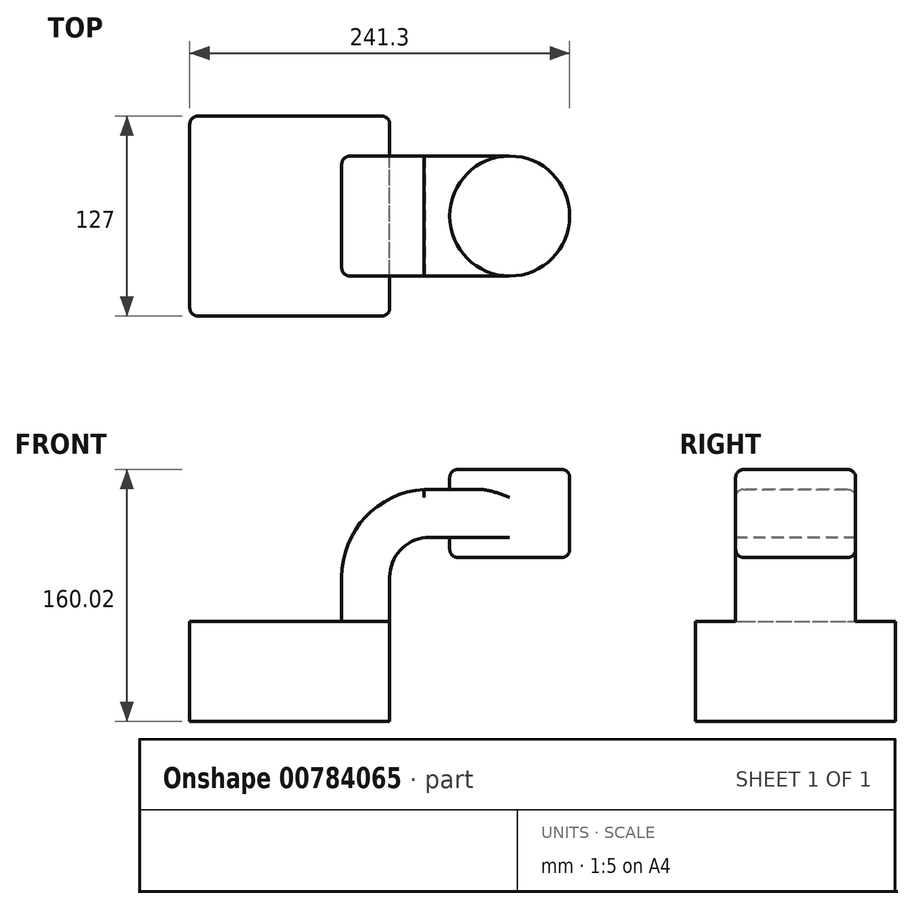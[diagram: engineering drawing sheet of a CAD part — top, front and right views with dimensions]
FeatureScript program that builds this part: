
annotation { "Feature Type Name" : "Feature", "Feature Type Description" : "" }
export const myFeature = defineFeature(function(context is Context, id is Id, definition is map)
    precondition{}
    {
        {
            var Q0;
            Q0=qCreatedBy(makeId("Front.planeOp"),FACE);
            var sketch = newSketch(context, id + "F0", { "sketchPlane" : qUnion([Q0])});
            skLineSegment(sketch, "E0.bottom", {"start": v(63.5, 31.75) * mm, "end": v(-63.5, 31.75) * mm});
            skLineSegment(sketch, "E0.top", {"start": v(63.5, -31.75) * mm, "end": v(-63.5, -31.75) * mm});
            skLineSegment(sketch, "E0.left", {"start": v(63.5, 31.75) * mm, "end": v(63.5, -31.75) * mm});
            skLineSegment(sketch, "E0.right", {"start": v(-63.5, 31.75) * mm, "end": v(-63.5, -31.75) * mm});
            skPoint(sketch, "E0.middle", {"position": v(0, 0) * mm});
            skLineSegment(sketch, "E1.bottom", {"start": v(177.8, 128.27) * mm, "end": v(101.6, 128.27) * mm});
            skLineSegment(sketch, "E1.top", {"start": v(177.8, 72.4) * mm, "end": v(101.6, 72.4) * mm});
            skLineSegment(sketch, "E1.left", {"start": v(177.8, 128.27) * mm, "end": v(177.8, 72.4) * mm});
            skLineSegment(sketch, "E1.right", {"start": v(101.6, 128.27) * mm, "end": v(101.6, 72.4) * mm});
            skPoint(sketch, "E1.middle", {"position": v(139.7, 100.33) * mm});
            skLineSegment(sketch, "E2", {"start": v(63.5, 31.75) * mm, "end": v(63.5, 59.92) * mm});
            skArc(sketch, "E3", {"start": v(63.5, 59.92) * mm, "mid": v(70.06, 76.96) * mm, "end": v(86.36, 85.2) * mm});
            skLineSegment(sketch, "E4", {"start": v(86.36, 85.2) * mm, "end": v(139.7, 85.2) * mm});
            skLineSegment(sketch, "E5.0", {"start": v(85.13, 115.68) * mm, "end": v(139.7, 115.68) * mm});
            skArc(sketch, "E5.1", {"start": v(33.02, 59.92) * mm, "mid": v(48.08, 98.08) * mm, "end": v(85.13, 115.68) * mm});
            skLineSegment(sketch, "E5.2", {"start": v(33.02, 31.75) * mm, "end": v(33.02, 59.92) * mm});
            skLineSegment(sketch, "E6", {"start": v(139.7, 72.4) * mm, "end": v(139.7, 128.27) * mm});
            skFitSpline(sketch, "E7", {"points": [v(-63.5, 31.75) * mm, v(85.13, 115.68) * mm], "startDerivative": vector(64.72, 185.3) * mm, "endDerivative": vector(169.63, -1.96) * mm});
            skSolve(sketch);
        }
        {
            var Q0;
            Q0=makeQuery(id+"F0.imprint","IMPRINT",FACE,{"disambiguationData":[TD([[makeQuery(id+"F0.imprint","IMPRINT",EDGE,{"derivedFrom":sQuery(id+"F0.wireOp",EDGE,"E0.top")}),-1.0]])]});
            extrude(context, id + "F1", {"entities" : qUnion([Q0]), "endBound" : BoundingType.SYMMETRIC, "depth" : 127 * mm, "offsetDistance" : 25.4 * mm});
        }
        {
            var Q0;
            {var subQ1=sQuery(id+"F0.wireOp",EDGE,"E2");Q0=makeQuery(id+"F0.imprint","IMPRINT",FACE,{"disambiguationData":[TD([[makeQuery(id+"F0.imprint","IMPRINT",EDGE,{"derivedFrom":subQ1}),1.0]])]});}
            extrude(context, id + "F2", {"entities" : qUnion([Q0]), "operationType" : NewBodyOperationType.ADD, "endBound" : BoundingType.SYMMETRIC, "depth" : 76.2 * mm, "offsetDistance" : 25.4 * mm});
        }
        {
            var Q0;
            Q0=makeQuery(id+"F0.imprint","IMPRINT",FACE,{"disambiguationData":[TD([[makeQuery(id+"F0.imprint","IMPRINT",EDGE,{"derivedFrom":sQuery(id+"F0.wireOp",EDGE,"E5.1")}),1.0]])]});
            extrude(context, id + "F3", {"entities" : qUnion([Q0]), "operationType" : NewBodyOperationType.ADD, "endBound" : BoundingType.SYMMETRIC, "depth" : 19.05 * mm, "offsetDistance" : 25.4 * mm});
        }
        {
            var Q0;
            {var subQ0=sQuery(id+"F0.wireOp",EDGE,"E5.0");var subQ1=sQuery(id+"F0.wireOp",EDGE,"E1.right");var subQ2=makeQuery(id+"F0.imprint","INTERSECT",VERTEX,{"derivedFrom":[subQ1,subQ0]});Q0=makeQuery(id+"F0.imprint","IMPRINT",FACE,{"disambiguationData":[TD([[makeQuery(id+"F0.imprint","IMPRINT",EDGE,{"disambiguationData":[TD([[subQ2,-1.0]])],"derivedFrom":subQ1}),1.0]])]});}
            extrude(context, id + "F4", {"entities" : qUnion([Q0]), "operationType" : NewBodyOperationType.ADD, "endBound" : BoundingType.SYMMETRIC, "depth" : 76.2 * mm, "offsetDistance" : 25.4 * mm});
        }
        {
            var Q0;
            {var subQ4=sQuery(id+"F0.wireOp",EDGE,"E1.left");Q0=makeQuery(id+"F0.imprint","IMPRINT",FACE,{"disambiguationData":[TD([[makeQuery(id+"F0.imprint","IMPRINT",EDGE,{"derivedFrom":subQ4}),-1.0]])]});}
            var Q1;
            Q1=sQuery(id+"F0.wireOp",EDGE,"E6");
            revolve(context, id + "F5", {"operationType" : NewBodyOperationType.ADD, "surfaceOperationType" : NewSurfaceOperationType.NEW, "entities" : qUnion([Q0]), "axis" : qUnion([Q1]), "revolveType" : RevolveType.FULL});
        }
        {
            var Q0;
            Q0=makeQuery(id+"F1.opExtrude","CAP_EDGE",EDGE,{"disambiguationData":[OSD([sQuery(id+"F0.wireOp",EDGE,"E0.left")])],"isStart":false});
            var Q1;
            Q1=makeQuery(id+"F1.opExtrude","CAP_EDGE",EDGE,{"disambiguationData":[OSD([sQuery(id+"F0.wireOp",EDGE,"E0.right")])],"isStart":false});
            var Q2;
            Q2=makeQuery(id+"F3.opExtrude","CAP_EDGE",EDGE,{"disambiguationData":[OSD([sQuery(id+"F0.wireOp",EDGE,"E7")])],"isStart":false});
            var Q3;
            Q3=makeQuery(id+"F1.opExtrude","CAP_EDGE",EDGE,{"disambiguationData":[OSD([sQuery(id+"F0.wireOp",EDGE,"E0.left")])],"isStart":true});
            var Q4;
            Q4=makeQuery(id+"F3.opExtrude","CAP_EDGE",EDGE,{"disambiguationData":[OSD([sQuery(id+"F0.wireOp",EDGE,"E7")])],"isStart":true});
            var Q5;
            Q5=makeQuery(id+"F1.opExtrude","CAP_EDGE",EDGE,{"disambiguationData":[OSD([sQuery(id+"F0.wireOp",EDGE,"E0.right")])],"isStart":true});
            var Q6;
            Q6=makeQuery(id+"F2.opExtrude","CAP_EDGE",EDGE,{"disambiguationData":[OSD([sQuery(id+"F0.wireOp",EDGE,"E5.1")])],"isStart":true});
            var Q7;
            Q7=makeQuery(id+"F2.opExtrude","CAP_EDGE",EDGE,{"disambiguationData":[OSD([sQuery(id+"F0.wireOp",EDGE,"E5.2")])],"isStart":true});
            var Q8;
            {var subQ0=sQuery(id+"F0.wireOp",EDGE,"E5.0");Q8=makeQuery(id+"F4.boolean.opBoolean","MERGE",EDGE,{"derivedFrom":[makeQuery(id+"F2.opExtrude","CAP_EDGE",EDGE,{"disambiguationData":[OSD([subQ0])],"isStart":true}),makeQuery(id+"F4.opExtrude","CAP_EDGE",EDGE,{"disambiguationData":[OSD([subQ0])],"isStart":true})]});}
            var Q9;
            Q9=makeQuery(id+"F2.opExtrude","CAP_EDGE",EDGE,{"disambiguationData":[OSD([sQuery(id+"F0.wireOp",EDGE,"E5.1")])],"isStart":false});
            var Q10;
            Q10=makeQuery(id+"F2.opExtrude","CAP_EDGE",EDGE,{"disambiguationData":[OSD([sQuery(id+"F0.wireOp",EDGE,"E5.2")])],"isStart":false});
            var Q11;
            {var subQ0=sQuery(id+"F0.wireOp",EDGE,"E5.0");Q11=makeQuery(id+"F4.boolean.opBoolean","MERGE",EDGE,{"derivedFrom":[makeQuery(id+"F2.opExtrude","CAP_EDGE",EDGE,{"disambiguationData":[OSD([subQ0])],"isStart":false}),makeQuery(id+"F4.opExtrude","CAP_EDGE",EDGE,{"disambiguationData":[OSD([subQ0])],"isStart":false})]});}
            var Q12;
            Q12=makeQuery(id+"F5.opRevolve","SWEPT_EDGE",EDGE,{"disambiguationData":[OSD([sQuery(id+"F0.wireOp",EDGE,"E1.bottom"),sQuery(id+"F0.wireOp",EDGE,"E1.left")])]});
            var Q13;
            Q13=makeQuery(id+"F5.opRevolve","SWEPT_EDGE",EDGE,{"disambiguationData":[OSD([sQuery(id+"F0.wireOp",EDGE,"E1.top"),sQuery(id+"F0.wireOp",EDGE,"E1.left")])]});
            fillet(context, id + "F6", {"entities" : qUnion([Q0, Q1, Q2, Q3, Q4, Q5, Q6, Q7, Q8, Q9, Q10, Q11, Q12, Q13]), "radius" : 5.08 * mm, "tangentPropagation" : true, "allowEdgeOverflow" : false});
        }
    });
